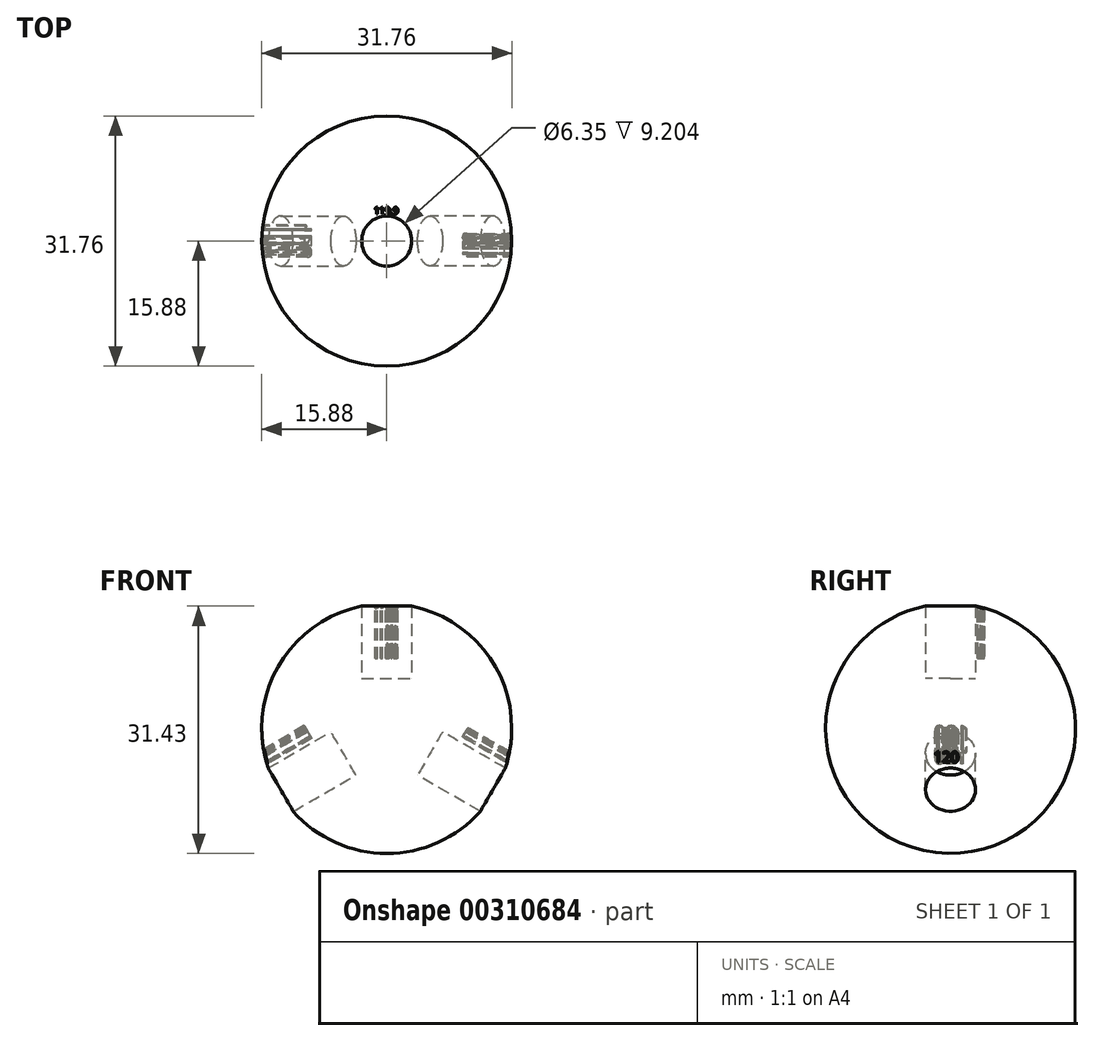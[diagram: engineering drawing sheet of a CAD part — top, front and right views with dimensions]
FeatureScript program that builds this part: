
annotation { "Feature Type Name" : "Feature", "Feature Type Description" : "" }
export const myFeature = defineFeature(function(context is Context, id is Id, definition is map)
    precondition{}
    {
        {
            var Q0;
            Q0=qCreatedBy(makeId("Front.planeOp"),FACE);
            var sketch = newSketch(context, id + "F0", { "sketchPlane" : qUnion([Q0])});
            skArc(sketch, "E0", {"start": v(-15.88, 0) * mm, "mid": v(0, -15.88) * mm, "end": v(15.88, 0) * mm});
            skLineSegment(sketch, "E1", {"start": v(15.88, 0) * mm, "end": v(-15.88, 0) * mm});
            skSolve(sketch);
        }
        {
            var Q0;
            Q0=qCreatedBy(makeId("Right.planeOp"),FACE);
            var sketch = newSketch(context, id + "F1", { "sketchPlane" : qUnion([Q0])});
            skCircle(sketch, "E2", {"center": v(0, 0) * mm, "radius": 15.88 * mm});
            skSolve(sketch);
        }
        {
            var Q0;
            Q0 = qSketchRegion(id + "F0", true);
            var Q1;
            Q1=sQuery(id+"F1.wireOp",EDGE,"E2");
            revolve(context, id + "F2", {"entities" : qUnion([Q0]), "axis" : qUnion([Q1]), "revolveType" : RevolveType.FULL});
        }
        {
            var Q0;
            Q0=qCreatedBy(makeId("Top.planeOp"),FACE);
            cPlane(context, id + "F3", {"entities" : qUnion([Q0]), "cplaneType" : CPlaneType.OFFSET, "offset" : 6.35 * mm, "width" : 152.4 * mm, "height" : 152.4 * mm});
        }
        {
            var Q0;
            Q0=qCreatedBy(id+"F3.planeOp",FACE);
            var sketch = newSketch(context, id + "F4", { "sketchPlane" : qUnion([Q0])});
            skCircle(sketch, "E3", {"center": v(0, 0) * mm, "radius": 3.18 * mm});
            skSolve(sketch);
        }
        {
            var Q0;
            Q0 = qSketchRegion(id + "F4", true);
            extrude(context, id + "F5", {"entities" : qUnion([Q0]), "depth" : 25.4 * mm});
        }
        {
            var Q0;
            Q0=makeQuery(id+"F5.opExtrude","CAP_FACE",FACE,{"disambiguationData":[OSD([sQuery(id+"F4.wireOp",EDGE,"E3")])],"isStart":false});
            cPlane(context, id + "F6", {"entities" : qUnion([Q0]), "cplaneType" : CPlaneType.OFFSET, "offset" : 12.7 * mm, "oppositeDirection" : true, "width" : 152.4 * mm, "height" : 152.4 * mm});
        }
        {
            var Q0;
            Q0=qCreatedBy(id+"F6.planeOp",FACE);
            var sketch = newSketch(context, id + "F7", { "sketchPlane" : qUnion([Q0])});
            skText(sketch, "E4", { "text": "119.9", "fontName": "OpenSans-Regular.ttf"});
            const initialGuessF7  = {"E4": [-0.00163, 0.00341, 1, 0, 0.00088]};
            skSetInitialGuess(sketch, initialGuessF7);
            skSolve(sketch);
        }
        {
            var Q0;
            Q0 = qSketchRegion(id + "F7", true);
            extrude(context, id + "F8", {"entities" : qUnion([Q0]), "operationType" : NewBodyOperationType.REMOVE, "oppositeDirection" : true, "depth" : 10.16 * mm});
        }
        {
            var Q0;
            Q0=qCreatedBy(makeId("Right.planeOp"),FACE);
            var sketch = newSketch(context, id + "F9", { "sketchPlane" : qUnion([Q0])});
            skLineSegment(sketch, "E5", {"start": v(50.33, 0) * mm, "end": v(-60.1, 0) * mm, "construction": true});
            skSolve(sketch);
        }
        {
            var Q0;
            Q0=makeQuery(id+"F5.opExtrude","SWEPT_BODY",BODY,{"disambiguationData":[OSD([sQuery(id+"F4.wireOp",EDGE,"E3")])]});
            var Q1;
            Q1=sQuery(id+"F9.wireOp",EDGE,"E5");
            transform(context, id + "F10", {"entities" : qUnion([Q0]), "transformType" : TransformType.ROTATION, "transformAxis" : qUnion([Q1]), "angle" : 120 * degree, "makeCopy" : true});
        }
        {
            var Q0;
            Q0=makeQuery(id+"F10.opPattern","COPY",FACE,{"derivedFrom":makeQuery(id+"F5.opExtrude","CAP_FACE",FACE,{"disambiguationData":[OSD([sQuery(id+"F4.wireOp",EDGE,"E3")])],"isStart":false}),"instanceName":"1"});
            cPlane(context, id + "F11", {"entities" : qUnion([Q0]), "cplaneType" : CPlaneType.OFFSET, "offset" : 12.7 * mm, "oppositeDirection" : true, "width" : 152.4 * mm, "height" : 152.4 * mm});
        }
        {
            var Q0;
            Q0=qCreatedBy(id+"F11.planeOp",FACE);
            var sketch = newSketch(context, id + "F12", { "sketchPlane" : qUnion([Q0])});
            skText(sketch, "E6", { "text": "120\n", "fontName": "OpenSans-Regular.ttf"});
            const initialGuessF12  = {"E6": [-0.00223, 0.0037, 1, 0, 0.00184]};
            skSetInitialGuess(sketch, initialGuessF12);
            skSolve(sketch);
        }
        {
            var Q0;
            Q0 = qSketchRegion(id + "F12", true);
            extrude(context, id + "F13", {"entities" : qUnion([Q0]), "operationType" : NewBodyOperationType.REMOVE, "oppositeDirection" : true, "depth" : 10.16 * mm});
        }
        {
            var Q0;
            Q0=qCreatedBy(makeId("Right.planeOp"),FACE);
            var sketch = newSketch(context, id + "F14", { "sketchPlane" : qUnion([Q0])});
            skLineSegment(sketch, "E7", {"start": v(61.76, 0) * mm, "end": v(-32.63, 0) * mm, "construction": true});
            skSolve(sketch);
        }
        {
            var Q0;
            Q0=makeQuery(id+"F5.opExtrude","SWEPT_BODY",BODY,{"disambiguationData":[OSD([sQuery(id+"F4.wireOp",EDGE,"E3")])]});
            var Q1;
            Q1=sQuery(id+"F14.wireOp",EDGE,"E7");
            transform(context, id + "F15", {"entities" : qUnion([Q0]), "transformType" : TransformType.ROTATION, "transformAxis" : qUnion([Q1]), "angle" : 120 * degree, "oppositeDirection" : true, "makeCopy" : true});
        }
        {
            var Q0;
            Q0=makeQuery(id+"F15.opPattern","COPY",FACE,{"derivedFrom":makeQuery(id+"F5.opExtrude","CAP_FACE",FACE,{"disambiguationData":[OSD([sQuery(id+"F4.wireOp",EDGE,"E3")])],"isStart":false}),"instanceName":"1"});
            cPlane(context, id + "F16", {"entities" : qUnion([Q0]), "cplaneType" : CPlaneType.OFFSET, "offset" : 12.7 * mm, "oppositeDirection" : true, "width" : 152.4 * mm, "height" : 152.4 * mm});
        }
        {
            var Q0;
            Q0=qCreatedBy(id+"F16.planeOp",FACE);
            var sketch = newSketch(context, id + "F17", { "sketchPlane" : qUnion([Q0])});
            skText(sketch, "E8", { "text": "120\n", "fontName": "OpenSans-Regular.ttf"});
            const initialGuessF17  = {"E8": [-0.00213, 0.0039, 1, 0, 0.00134]};
            skSetInitialGuess(sketch, initialGuessF17);
            skSolve(sketch);
        }
        {
            var Q0;
            Q0 = qSketchRegion(id + "F17", true);
            extrude(context, id + "F18", {"entities" : qUnion([Q0]), "operationType" : NewBodyOperationType.REMOVE, "oppositeDirection" : true, "depth" : 10.16 * mm});
        }
        {
            var Q0;
            Q0=makeQuery(id+"F5.opExtrude","SWEPT_BODY",BODY,{"disambiguationData":[OSD([sQuery(id+"F4.wireOp",EDGE,"E3")])]});
            var Q1;
            Q1=makeQuery(id+"F15.opPattern","COPY",BODY,{"derivedFrom":makeQuery(id+"F5.opExtrude","SWEPT_BODY",BODY,{"disambiguationData":[OSD([sQuery(id+"F4.wireOp",EDGE,"E3")])]}),"instanceName":"1"});
            var Q2;
            Q2=makeQuery(id+"F10.opPattern","COPY",BODY,{"derivedFrom":makeQuery(id+"F5.opExtrude","SWEPT_BODY",BODY,{"disambiguationData":[OSD([sQuery(id+"F4.wireOp",EDGE,"E3")])]}),"instanceName":"1"});
            var Q3;
            Q3=makeQuery(id+"F2.opRevolve","SWEPT_BODY",BODY,{"disambiguationData":[OSD([sQuery(id+"F0.wireOp",EDGE,"E0"),sQuery(id+"F0.wireOp",EDGE,"E1")])]});
            booleanBodies(context, id + "F19", {"operationType" : BooleanOperationType.SUBTRACTION, "tools" : qUnion([Q0, Q1, Q2]), "targets" : qUnion([Q3])});
        }
    });
